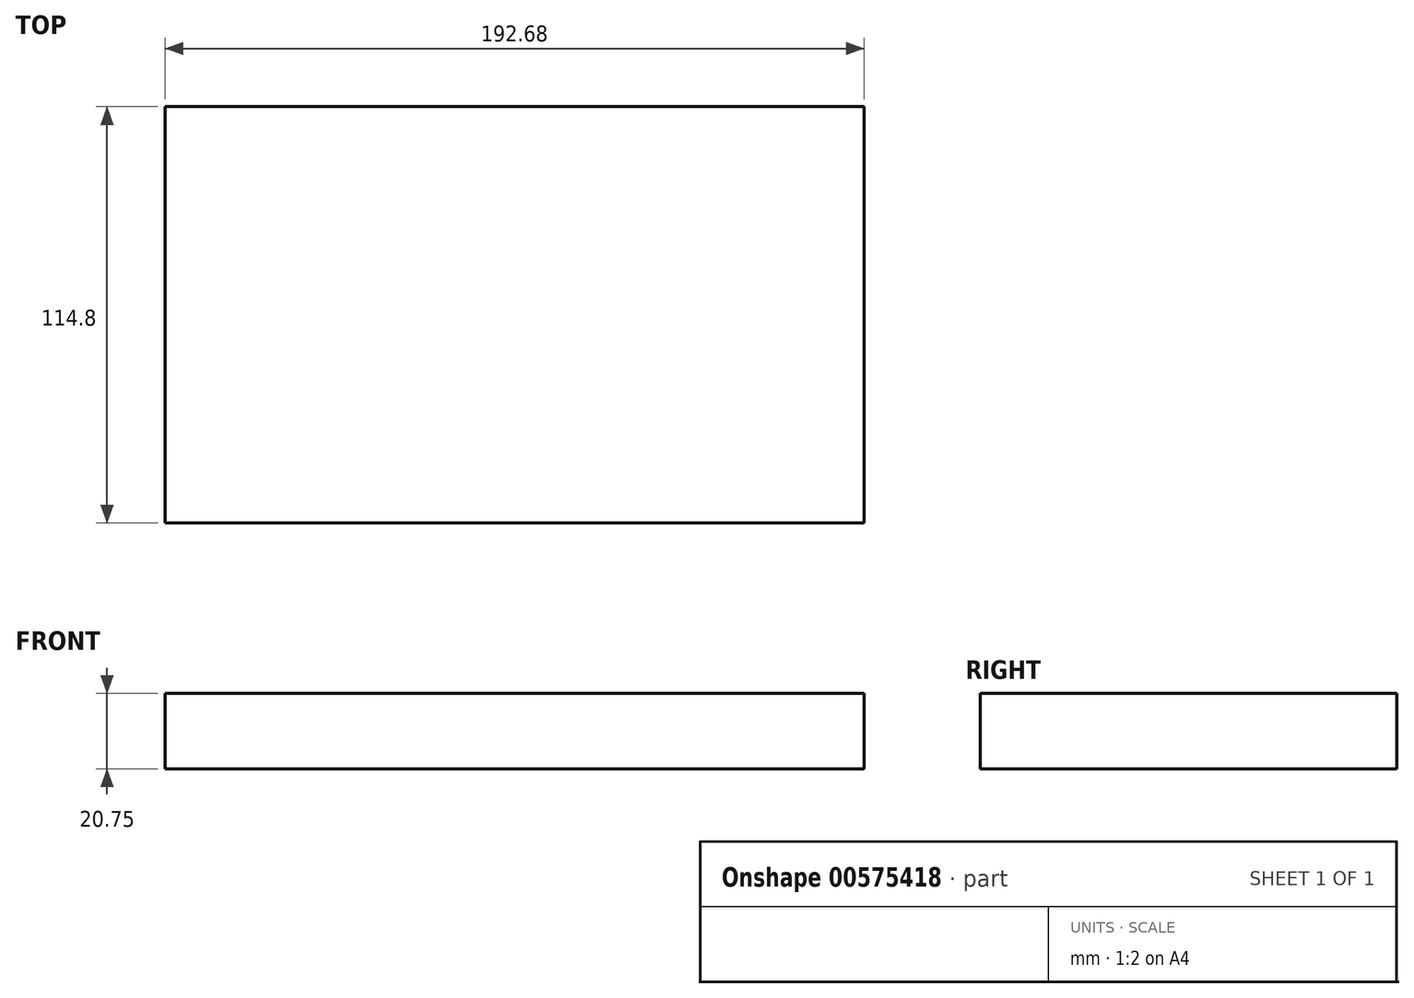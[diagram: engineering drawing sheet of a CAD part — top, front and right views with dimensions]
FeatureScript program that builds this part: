
annotation { "Feature Type Name" : "Feature", "Feature Type Description" : "" }
export const myFeature = defineFeature(function(context is Context, id is Id, definition is map)
    precondition{}
    {
        {
            var Q0;
            Q0=qCreatedBy(makeId("Top.planeOp"),FACE);
            var sketch = newSketch(context, id + "F0", { "sketchPlane" : qUnion([Q0])});
            skLineSegment(sketch, "E0.bottom", {"start": v(96.34, 57.4) * mm, "end": v(-96.34, 57.4) * mm});
            skLineSegment(sketch, "E0.top", {"start": v(96.34, -57.4) * mm, "end": v(-96.34, -57.4) * mm});
            skLineSegment(sketch, "E0.left", {"start": v(96.34, 57.4) * mm, "end": v(96.34, -57.4) * mm});
            skLineSegment(sketch, "E0.right", {"start": v(-96.34, 57.4) * mm, "end": v(-96.34, -57.4) * mm});
            skPoint(sketch, "E0.middle", {"position": v(0, 0) * mm});
            skSolve(sketch);
        }
        {
            var Q0;
            Q0=makeQuery(id+"F0.imprint","IMPRINT",FACE,{"disambiguationData":[TD([[makeQuery(id+"F0.imprint","IMPRINT",EDGE,{"derivedFrom":sQuery(id+"F0.wireOp",EDGE,"E0.bottom")}),1.0]])]});
            extrude(context, id + "F1", {"entities" : qUnion([Q0]), "depth" : 20.75 * mm, "offsetDistance" : 25.4 * mm});
        }
    });
